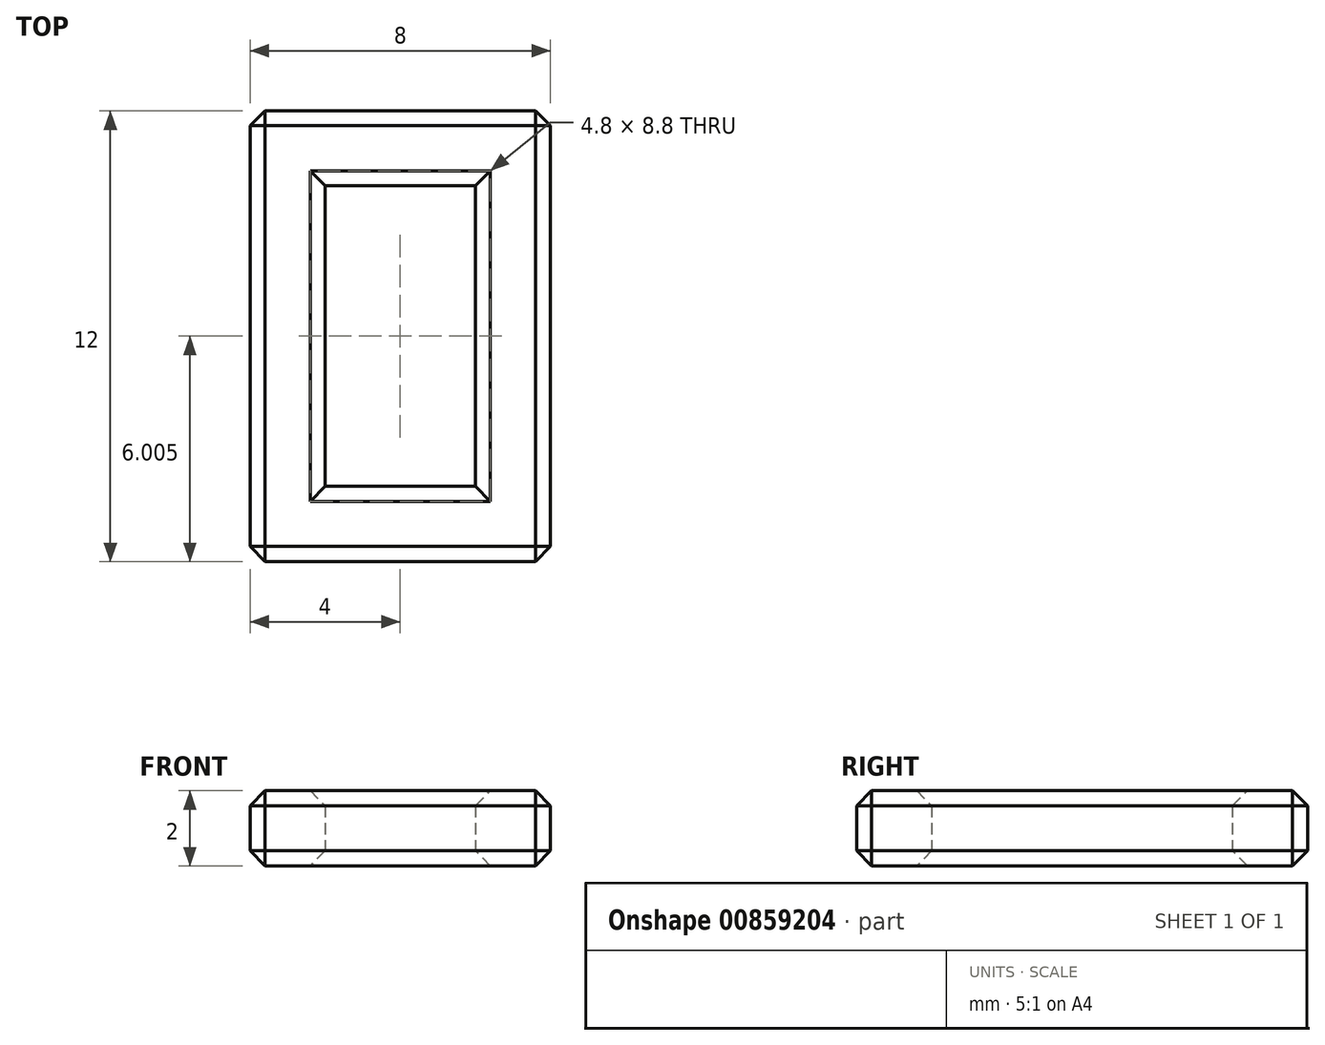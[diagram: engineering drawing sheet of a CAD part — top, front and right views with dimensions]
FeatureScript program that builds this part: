
annotation { "Feature Type Name" : "Feature", "Feature Type Description" : "" }
export const myFeature = defineFeature(function(context is Context, id is Id, definition is map)
    precondition{}
    {
        {
            var Q0;
            Q0=qCreatedBy(makeId("Top.planeOp"),FACE);
            var sketch = newSketch(context, id + "F0", { "sketchPlane" : qUnion([Q0])});
            skLineSegment(sketch, "E0.bottom", {"start": v(-14.33, -23.39) * mm, "end": v(-6.33, -23.39) * mm});
            skLineSegment(sketch, "E0.top", {"start": v(-14.33, -35.39) * mm, "end": v(-6.33, -35.39) * mm});
            skLineSegment(sketch, "E0.left", {"start": v(-14.33, -23.39) * mm, "end": v(-14.33, -35.39) * mm});
            skLineSegment(sketch, "E0.right", {"start": v(-6.33, -23.39) * mm, "end": v(-6.33, -35.39) * mm});
            skLineSegment(sketch, "E1.bottom", {"start": v(-12.33, -25.39) * mm, "end": v(-8.33, -25.39) * mm});
            skLineSegment(sketch, "E1.top", {"start": v(-12.33, -33.39) * mm, "end": v(-8.33, -33.39) * mm});
            skLineSegment(sketch, "E1.left", {"start": v(-12.33, -25.39) * mm, "end": v(-12.33, -33.39) * mm});
            skLineSegment(sketch, "E1.right", {"start": v(-8.33, -25.39) * mm, "end": v(-8.33, -33.39) * mm});
            skSolve(sketch);
        }
        {
            var Q0;
            Q0=qSketchRegion(id+"F0",true);
            extrude(context, id + "F1", {"entities" : qUnion([Q0]), "depth" : 2 * mm, "offsetDistance" : 25 * mm});
        }
        {
            var Q0;
            Q0=makeQuery(id+"F1.opExtrude","CAP_EDGE",EDGE,{"disambiguationData":[OSD([sQuery(id+"F0.wireOp",EDGE,"E1.right")])],"isStart":false});
            var Q1;
            Q1=makeQuery(id+"F1.opExtrude","CAP_EDGE",EDGE,{"disambiguationData":[OSD([sQuery(id+"F0.wireOp",EDGE,"E1.top")])],"isStart":false});
            var Q2;
            Q2=makeQuery(id+"F1.opExtrude","CAP_EDGE",EDGE,{"disambiguationData":[OSD([sQuery(id+"F0.wireOp",EDGE,"E1.left")])],"isStart":false});
            var Q3;
            Q3=makeQuery(id+"F1.opExtrude","CAP_EDGE",EDGE,{"disambiguationData":[OSD([sQuery(id+"F0.wireOp",EDGE,"E1.bottom")])],"isStart":false});
            var Q4;
            Q4=makeQuery(id+"F1.opExtrude","CAP_EDGE",EDGE,{"disambiguationData":[OSD([sQuery(id+"F0.wireOp",EDGE,"E0.top")])],"isStart":false});
            var Q5;
            Q5=makeQuery(id+"F1.opExtrude","CAP_EDGE",EDGE,{"disambiguationData":[OSD([sQuery(id+"F0.wireOp",EDGE,"E0.left")])],"isStart":false});
            var Q6;
            Q6=makeQuery(id+"F1.opExtrude","SWEPT_EDGE",EDGE,{"disambiguationData":[OSD([sQuery(id+"F0.wireOp",EDGE,"E0.top"),sQuery(id+"F0.wireOp",EDGE,"E0.left")])]});
            var Q7;
            Q7=makeQuery(id+"F1.opExtrude","SWEPT_EDGE",EDGE,{"disambiguationData":[OSD([sQuery(id+"F0.wireOp",EDGE,"E0.top"),sQuery(id+"F0.wireOp",EDGE,"E0.right")])]});
            var Q8;
            Q8=makeQuery(id+"F1.opExtrude","CAP_EDGE",EDGE,{"disambiguationData":[OSD([sQuery(id+"F0.wireOp",EDGE,"E0.right")])],"isStart":false});
            var Q9;
            Q9=makeQuery(id+"F1.opExtrude","CAP_EDGE",EDGE,{"disambiguationData":[OSD([sQuery(id+"F0.wireOp",EDGE,"E0.bottom")])],"isStart":false});
            var Q10;
            Q10=makeQuery(id+"F1.opExtrude","SWEPT_EDGE",EDGE,{"disambiguationData":[OSD([sQuery(id+"F0.wireOp",EDGE,"E0.bottom"),sQuery(id+"F0.wireOp",EDGE,"E0.right")])]});
            var Q11;
            Q11=makeQuery(id+"F1.opExtrude","SWEPT_EDGE",EDGE,{"disambiguationData":[OSD([sQuery(id+"F0.wireOp",EDGE,"E0.bottom"),sQuery(id+"F0.wireOp",EDGE,"E0.left")])]});
            var Q12;
            Q12=makeQuery(id+"F1.opExtrude","CAP_EDGE",EDGE,{"disambiguationData":[OSD([sQuery(id+"F0.wireOp",EDGE,"E0.left")])],"isStart":true});
            var Q13;
            Q13=makeQuery(id+"F1.opExtrude","CAP_EDGE",EDGE,{"disambiguationData":[OSD([sQuery(id+"F0.wireOp",EDGE,"E1.left")])],"isStart":true});
            var Q14;
            Q14=makeQuery(id+"F1.opExtrude","CAP_EDGE",EDGE,{"disambiguationData":[OSD([sQuery(id+"F0.wireOp",EDGE,"E1.bottom")])],"isStart":true});
            var Q15;
            Q15=makeQuery(id+"F1.opExtrude","CAP_EDGE",EDGE,{"disambiguationData":[OSD([sQuery(id+"F0.wireOp",EDGE,"E0.bottom")])],"isStart":true});
            var Q16;
            Q16=makeQuery(id+"F1.opExtrude","CAP_EDGE",EDGE,{"disambiguationData":[OSD([sQuery(id+"F0.wireOp",EDGE,"E0.right")])],"isStart":true});
            var Q17;
            Q17=makeQuery(id+"F1.opExtrude","CAP_EDGE",EDGE,{"disambiguationData":[OSD([sQuery(id+"F0.wireOp",EDGE,"E1.right")])],"isStart":true});
            var Q18;
            Q18=makeQuery(id+"F1.opExtrude","CAP_EDGE",EDGE,{"disambiguationData":[OSD([sQuery(id+"F0.wireOp",EDGE,"E1.top")])],"isStart":true});
            var Q19;
            Q19=makeQuery(id+"F1.opExtrude","CAP_EDGE",EDGE,{"disambiguationData":[OSD([sQuery(id+"F0.wireOp",EDGE,"E0.top")])],"isStart":true});
            chamfer(context, id + "F2", {"entities" : qUnion([Q0, Q1, Q2, Q3, Q4, Q5, Q6, Q7, Q8, Q9, Q10, Q11, Q12, Q13, Q14, Q15, Q16, Q17, Q18, Q19]), "width" : .4 * mm, "tangentPropagation" : true});
        }
    });
